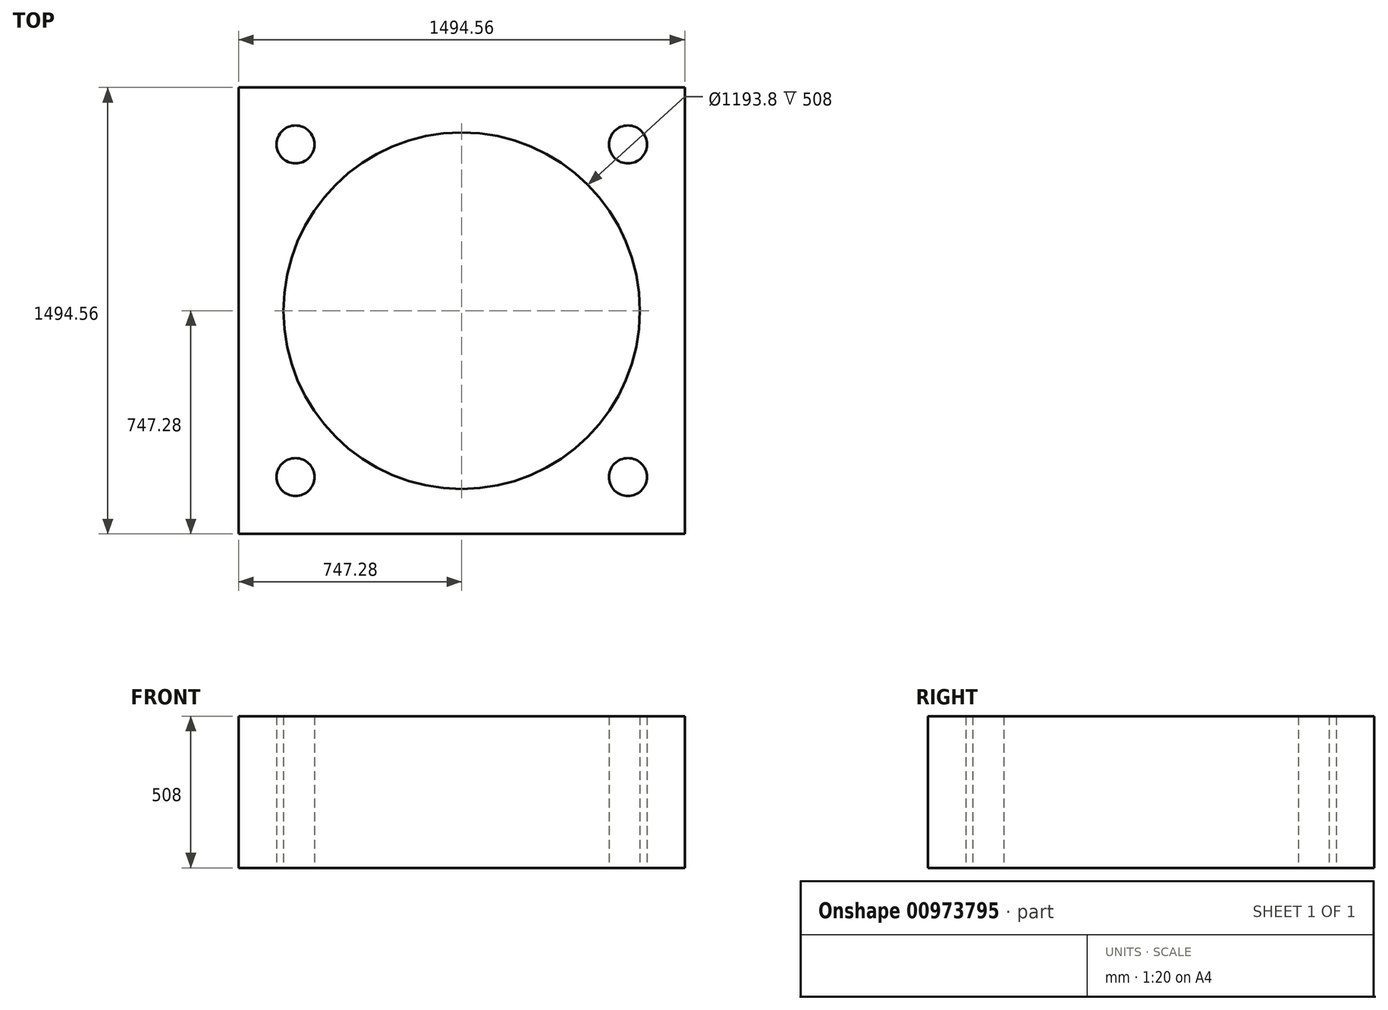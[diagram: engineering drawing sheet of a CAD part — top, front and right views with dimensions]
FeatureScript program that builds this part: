
annotation { "Feature Type Name" : "Feature", "Feature Type Description" : "" }
export const myFeature = defineFeature(function(context is Context, id is Id, definition is map)
    precondition{}
    {
        {
            var Q0;
            Q0=qCreatedBy(makeId("Top.planeOp"),FACE);
            var sketch = newSketch(context, id + "F0", { "sketchPlane" : qUnion([Q0])});
            skCircle(sketch, "E0", {"center": v(0, 0) * mm, "radius": 596.9 * mm});
            skLineSegment(sketch, "E1.bottom", {"start": v(-747.28, 747.28) * mm, "end": v(747.28, 747.28) * mm});
            skLineSegment(sketch, "E1.top", {"start": v(-747.28, -747.28) * mm, "end": v(747.28, -747.28) * mm});
            skLineSegment(sketch, "E1.left", {"start": v(-747.28, 747.28) * mm, "end": v(-747.28, -747.28) * mm});
            skLineSegment(sketch, "E1.right", {"start": v(747.28, 747.28) * mm, "end": v(747.28, -747.28) * mm});
            skCircle(sketch, "E2", {"center": v(556.78, 556.78) * mm, "radius": 63.5 * mm});
            skCircle(sketch, "E3", {"center": v(556.78, -556.78) * mm, "radius": 63.5 * mm});
            skCircle(sketch, "E4", {"center": v(-556.78, -556.78) * mm, "radius": 63.5 * mm});
            skCircle(sketch, "E5", {"center": v(-556.78, 556.78) * mm, "radius": 63.5 * mm});
            skLineSegment(sketch, "E6.bottom", {"start": v(-556.78, 556.78) * mm, "end": v(556.78, 556.78) * mm, "construction": true});
            skLineSegment(sketch, "E6.top", {"start": v(-556.78, -556.78) * mm, "end": v(556.78, -556.78) * mm, "construction": true});
            skLineSegment(sketch, "E6.left", {"start": v(-556.78, 556.78) * mm, "end": v(-556.78, -556.78) * mm, "construction": true});
            skLineSegment(sketch, "E6.right", {"start": v(556.78, 556.78) * mm, "end": v(556.78, -556.78) * mm, "construction": true});
            skLineSegment(sketch, "E7", {"start": v(-747.28, 747.28) * mm, "end": v(747.28, -747.28) * mm});
            skLineSegment(sketch, "E8", {"start": v(-556.78, -556.78) * mm, "end": v(556.78, 556.78) * mm});
            skCircle(sketch, "E9", {"center": v(556.78, 556.78) * mm, "radius": 190.5 * mm, "construction": true});
            skSolve(sketch);
        }
        {
            var Q0;
            Q0 = qSketchRegion(id + "F0", true);
            extrude(context, id + "F1", {"entities" : qUnion([Q0]), "depth" : 508 * mm, "offsetDistance" : 25.4 * mm});
        }
    });
